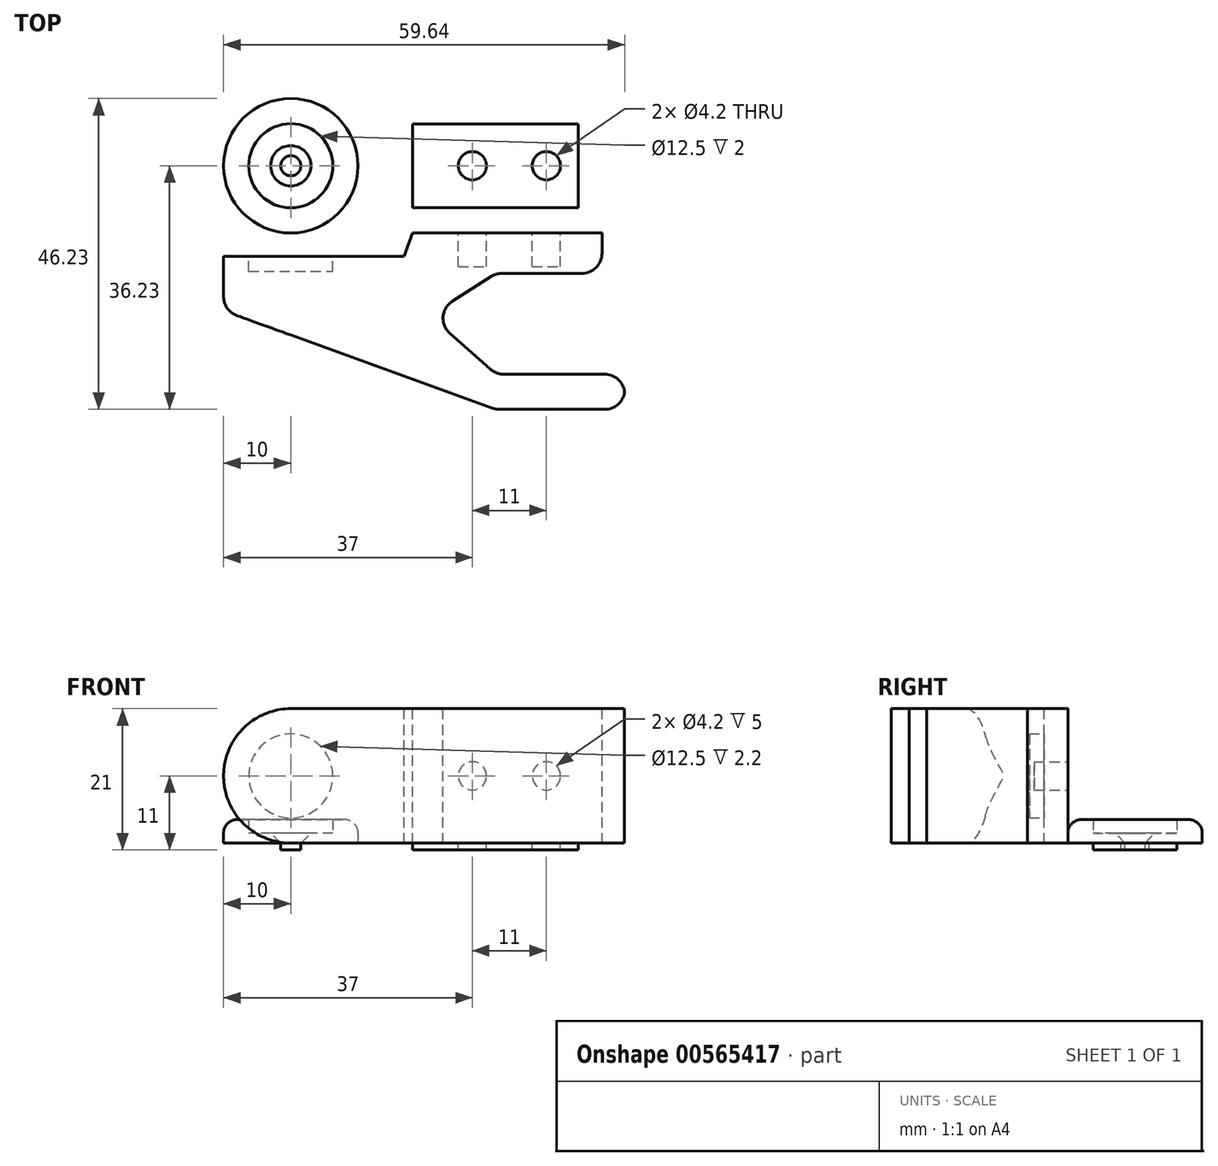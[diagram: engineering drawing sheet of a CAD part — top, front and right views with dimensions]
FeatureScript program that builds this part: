
annotation { "Feature Type Name" : "Feature", "Feature Type Description" : "" }
export const myFeature = defineFeature(function(context is Context, id is Id, definition is map)
    precondition{}
    {
        {
            var Q0;
            Q0=qCreatedBy(makeId("Top.planeOp"),FACE);
            var sketch = newSketch(context, id + "F0", { "sketchPlane" : qUnion([Q0])});
            skPoint(sketch, "E0", {"position": v(-15, 0) * mm});
            skPoint(sketch, "E1", {"position": v(15, 0) * mm});
            skCircle(sketch, "E2", {"center": v(-15, 0) * mm, "radius": 1.5 * mm});
            skCircle(sketch, "E3", {"center": v(-15, 0) * mm, "radius": 10 * mm});
            skCircle(sketch, "E4", {"center": v(-15, 0) * mm, "radius": 6.25 * mm});
            skSolve(sketch);
        }
        {
            var Q0;
            Q0=makeQuery(id+"F0.imprint","IMPRINT",FACE,{"disambiguationData":[TD([[makeQuery(id+"F0.imprint","IMPRINT",EDGE,{"derivedFrom":sQuery(id+"F0.wireOp",EDGE,"E3")}),1.0]])]});
            var Q1;
            Q1=makeQuery(id+"F0.imprint","IMPRINT",FACE,{"disambiguationData":[TD([[makeQuery(id+"F0.imprint","IMPRINT",EDGE,{"derivedFrom":sQuery(id+"F0.wireOp",EDGE,"E2")}),-1.0]])]});
            extrude(context, id + "F1", {"entities" : qUnion([Q0, Q1]), "depth" : 1.5 * mm, "offsetDistance" : 25 * mm});
        }
        {
            var Q0;
            Q0=makeQuery(id+"F1.opExtrude","CAP_EDGE",EDGE,{"disambiguationData":[OSD([sQuery(id+"F0.wireOp",EDGE,"E2")])],"isStart":false});
            chamfer(context, id + "F2", {"entities" : qUnion([Q0]), "width" : 1.5 * mm, "tangentPropagation" : true});
        }
        {
            var Q0;
            Q0=makeQuery(id+"F1.opExtrude","CAP_FACE",FACE,{"disambiguationData":[OSD([sQuery(id+"F0.wireOp",EDGE,"E2"),sQuery(id+"F0.wireOp",EDGE,"E3")])],"isStart":false});
            var sketch = newSketch(context, id + "F3", { "sketchPlane" : qUnion([Q0])});
            skCircle(sketch, "E5.0", {"center": v(-15, 0) * mm, "radius": 6.25 * mm});
            skCircle(sketch, "E6.0", {"center": v(-15, 0) * mm, "radius": 10 * mm});
            skSolve(sketch);
        }
        {
            var Q0;
            Q0=makeQuery(id+"F3.imprint","IMPRINT",FACE,{"disambiguationData":[TD([[makeQuery(id+"F3.imprint","IMPRINT",EDGE,{"derivedFrom":sQuery(id+"F3.wireOp",EDGE,"E5.0")}),-1.0]])]});
            extrude(context, id + "F4", {"entities" : qUnion([Q0]), "operationType" : NewBodyOperationType.ADD, "depth" : 2 * mm, "offsetDistance" : 25 * mm});
        }
        {
            var Q0;
            Q0=makeQuery(id+"F4.opExtrude","CAP_EDGE",EDGE,{"disambiguationData":[OSD([sQuery(id+"F3.wireOp",EDGE,"E6.0")])],"isStart":false});
            fillet(context, id + "F5", {"entities" : qUnion([Q0]), "radius" : 2 * mm, "tangentPropagation" : true, "allowEdgeOverflow" : false});
        }
        {
            var Q0;
            Q0=qCreatedBy(makeId("Front.planeOp"),FACE);
            var sketch = newSketch(context, id + "F6", { "sketchPlane" : qUnion([Q0])});
            skLineSegment(sketch, "E7.0", {"start": v(-23, 3.5) * mm, "end": v(-21.25, 3.5) * mm});
            skLineSegment(sketch, "E8", {"start": v(-23.02, 12.27) * mm, "end": v(15.04, 26.06) * mm});
            skLineSegment(sketch, "E9", {"start": v(16.06, 26.23) * mm, "end": v(31.66, 26.23) * mm});
            skLineSegment(sketch, "E10", {"start": v(34.66, 24) * mm, "end": v(34.66, 23.23) * mm});
            skLineSegment(sketch, "E11", {"start": v(31.66, 21) * mm, "end": v(16.67, 21) * mm});
            skLineSegment(sketch, "E12", {"start": v(14.68, 20.25) * mm, "end": v(8.65, 14.92) * mm});
            skLineSegment(sketch, "E13", {"start": v(9.03, 10.14) * mm, "end": v(14.8, 6.47) * mm});
            skLineSegment(sketch, "E14", {"start": v(16.4, 6) * mm, "end": v(28.27, 6) * mm});
            skLineSegment(sketch, "E15", {"start": v(31.27, 3) * mm, "end": v(31.27, 0) * mm});
            skLineSegment(sketch, "E16", {"start": v(31.27, 0) * mm, "end": v(3.08, 0) * mm});
            skLineSegment(sketch, "E17", {"start": v(3.08, 0) * mm, "end": v(1.81, 3.5) * mm});
            skLineSegment(sketch, "E18", {"start": v(1.81, 3.5) * mm, "end": v(-7, 3.5) * mm});
            skPoint(sketch, "E19.visualSharp", {"position": v(15.54, 21) * mm});
            skArc(sketch, "E19.filletArc", {"start": v(16.67, 21) * mm, "mid": v(15.6, 20.8) * mm, "end": v(14.68, 20.25) * mm});
            skPoint(sketch, "E20.visualSharp", {"position": v(5.66, 12.28) * mm});
            skArc(sketch, "E20.filletArc", {"start": v(8.65, 14.92) * mm, "mid": v(7.65, 12.43) * mm, "end": v(9.03, 10.14) * mm});
            skPoint(sketch, "E21.visualSharp", {"position": v(15.54, 6) * mm});
            skArc(sketch, "E21.filletArc", {"start": v(14.8, 6.47) * mm, "mid": v(15.57, 6.12) * mm, "end": v(16.4, 6) * mm});
            skPoint(sketch, "E22.visualSharp", {"position": v(31.27, 6) * mm});
            skArc(sketch, "E22.filletArc", {"start": v(31.27, 3) * mm, "mid": v(30.4, 5.12) * mm, "end": v(28.27, 6) * mm});
            skPoint(sketch, "E23.visualSharp", {"position": v(15.54, 26.23) * mm});
            skArc(sketch, "E23.filletArc", {"start": v(16.06, 26.23) * mm, "mid": v(15.54, 26.19) * mm, "end": v(15.04, 26.06) * mm});
            skPoint(sketch, "E24.visualSharp", {"position": v(-23, 12.28) * mm});
            skArc(sketch, "E24.filletArc", {"start": v(-23.02, 12.27) * mm, "mid": v(-24.46, 11.17) * mm, "end": v(-25, 9.45) * mm});
            skPoint(sketch, "E25.visualSharp", {"position": v(34.66, 26.23) * mm});
            skArc(sketch, "E25.filletArc", {"start": v(34.66, 23.23) * mm, "mid": v(33.78, 25.36) * mm, "end": v(31.66, 26.23) * mm});
            skPoint(sketch, "E26.visualSharp", {"position": v(34.66, 21) * mm});
            skArc(sketch, "E26.filletArc", {"start": v(31.66, 21) * mm, "mid": v(33.78, 21.88) * mm, "end": v(34.66, 24) * mm});
            skLineSegment(sketch, "E27", {"start": v(-8.75, 3.5) * mm, "end": v(-7, 3.5) * mm});
            skLineSegment(sketch, "E28", {"start": v(-21.25, 3.5) * mm, "end": v(-21.25, 5.7) * mm});
            skLineSegment(sketch, "E29", {"start": v(-21.25, 5.7) * mm, "end": v(-8.75, 5.7) * mm});
            skLineSegment(sketch, "E30", {"start": v(-8.75, 5.7) * mm, "end": v(-8.75, 3.5) * mm});
            skLineSegment(sketch, "E31", {"start": v(-21.25, 3.5) * mm, "end": v(-8.75, 3.5) * mm});
            skLineSegment(sketch, "E32", {"start": v(-25, 9.45) * mm, "end": v(-25, 3.5) * mm});
            skLineSegment(sketch, "E33.0", {"start": v(-25, 0) * mm, "end": v(-5, 0) * mm, "construction": true});
            skLineSegment(sketch, "E34", {"start": v(-25, 3.5) * mm, "end": v(-23, 3.5) * mm});
            skSolve(sketch);
        }
        {
            var Q0;
            Q0=makeQuery(id+"F6.imprint","IMPRINT",FACE,{"disambiguationData":[TD([[makeQuery(id+"F6.imprint","IMPRINT",EDGE,{"derivedFrom":sQuery(id+"F6.wireOp",EDGE,"E7.0")}),1.0]])]});
            var Q1;
            Q1=makeQuery(id+"F6.imprint","IMPRINT",FACE,{"disambiguationData":[TD([[makeQuery(id+"F6.imprint","IMPRINT",EDGE,{"derivedFrom":sQuery(id+"F6.wireOp",EDGE,"E28")}),-1.0]])]});
            extrude(context, id + "F7", {"entities" : qUnion([Q0, Q1]), "endBound" : BoundingType.SYMMETRIC, "depth" : 20 * mm, "offsetDistance" : 25 * mm});
        }
        {
            var Q0;
            Q0=makeQuery(id+"F7.opExtrude","SWEPT_FACE",FACE,{"disambiguationData":[OSD([sQuery(id+"F6.wireOp",EDGE,"E16")])]});
            var sketch = newSketch(context, id + "F8", { "sketchPlane" : qUnion([Q0])});
            skCircle(sketch, "E35", {"center": v(12, 0) * mm, "radius": 2.1 * mm});
            skPoint(sketch, "E35.centerSnap0", {"position": v(3.08, 0) * mm});
            skCircle(sketch, "E36", {"center": v(23, 0) * mm, "radius": 2.1 * mm});
            skSolve(sketch);
        }
        {
            var Q0;
            Q0=makeQuery(id+"F8.imprint","IMPRINT",FACE,{"disambiguationData":[TD([[makeQuery(id+"F8.imprint","IMPRINT",EDGE,{"derivedFrom":sQuery(id+"F8.wireOp",EDGE,"E35")}),1.0]])]});
            var Q1;
            Q1=makeQuery(id+"F8.imprint","IMPRINT",FACE,{"disambiguationData":[TD([[makeQuery(id+"F8.imprint","IMPRINT",EDGE,{"derivedFrom":sQuery(id+"F8.wireOp",EDGE,"E36")}),1.0]])]});
            extrude(context, id + "F9", {"entities" : qUnion([Q0, Q1]), "operationType" : NewBodyOperationType.REMOVE, "oppositeDirection" : true, "depth" : 5 * mm, "offsetDistance" : 25 * mm});
        }
        {
            var Q0;
            Q0=makeQuery(id+"F7.opExtrude","SWEPT_FACE",FACE,{"disambiguationData":[OSD([sQuery(id+"F6.wireOp",EDGE,"E7.0"),sQuery(id+"F6.wireOp",EDGE,"E18"),sQuery(id+"F6.wireOp",EDGE,"E27"),sQuery(id+"F6.wireOp",EDGE,"E31"),sQuery(id+"F6.wireOp",EDGE,"E34")])]});
            var sketch = newSketch(context, id + "F10", { "sketchPlane" : qUnion([Q0])});
            skCircle(sketch, "E37.0", {"center": v(-15, 0) * mm, "radius": 10 * mm});
            skCircle(sketch, "E38.0", {"center": v(-15, 0) * mm, "radius": 6.25 * mm});
            skSolve(sketch);
        }
        {
            var Q0;
            {var subQ0=sQuery(id+"F10.wireOp",EDGE,"E37.0");var subQ1=sQuery(id+"F6.wireOp",EDGE,"E34");var subQ2=makeQuery(id+"F7.opExtrude","SWEPT_EDGE",EDGE,{"disambiguationData":[OSD([sQuery(id+"F6.wireOp",EDGE,"E32"),subQ1])]});var subQ3=makeQuery(id+"F10.imprint","INTERSECT",VERTEX,{"derivedFrom":[subQ2,subQ0]});Q0=makeQuery(id+"F10.imprint","IMPRINT",FACE,{"disambiguationData":[TD([[makeQuery(id+"F10.imprint","IMPRINT",EDGE,{"disambiguationData":[TD([[subQ3,1.0]])],"derivedFrom":subQ0}),-1.0]])]});}
            var Q1;
            {var subQ0=sQuery(id+"F10.wireOp",EDGE,"E37.0");var subQ1=sQuery(id+"F6.wireOp",EDGE,"E34");var subQ2=makeQuery(id+"F7.opExtrude","SWEPT_EDGE",EDGE,{"disambiguationData":[OSD([sQuery(id+"F6.wireOp",EDGE,"E32"),subQ1])]});var subQ3=makeQuery(id+"F10.imprint","INTERSECT",VERTEX,{"derivedFrom":[subQ2,subQ0]});Q1=makeQuery(id+"F10.imprint","IMPRINT",FACE,{"disambiguationData":[TD([[makeQuery(id+"F10.imprint","IMPRINT",EDGE,{"disambiguationData":[TD([[subQ3,-1.0]])],"derivedFrom":subQ0}),-1.0]])]});}
            extrude(context, id + "F11", {"entities" : qUnion([Q0, Q1]), "operationType" : NewBodyOperationType.REMOVE, "endBound" : BoundingType.THROUGH_ALL, "oppositeDirection" : true, "depth" : 25 * mm, "offsetDistance" : 25 * mm});
        }
        {
            var Q0;
            Q0=makeQuery(id+"F10.imprint","IMPRINT",FACE,{"disambiguationData":[TD([[makeQuery(id+"F10.imprint","IMPRINT",EDGE,{"derivedFrom":sQuery(id+"F10.wireOp",EDGE,"E38.0")}),1.0]])]});
            extrude(context, id + "F12", {"entities" : qUnion([Q0]), "operationType" : NewBodyOperationType.REMOVE, "oppositeDirection" : true, "depth" : 2.2 * mm, "offsetDistance" : 25 * mm});
        }
        {
            var Q0;
            Q0=makeQuery(id+"F7.opExtrude","SWEPT_FACE",FACE,{"disambiguationData":[OSD([sQuery(id+"F6.wireOp",EDGE,"E16")])]});
            var sketch = newSketch(context, id + "F13", { "sketchPlane" : qUnion([Q0])});
            skCircle(sketch, "E39.0", {"center": v(-15, 0) * mm, "radius": 1.5 * mm});
            skCircle(sketch, "E40.0", {"center": v(12, 0) * mm, "radius": 2.1 * mm, "construction": true});
            skCircle(sketch, "E41.0", {"center": v(23, 0) * mm, "radius": 2.1 * mm, "construction": true});
            skLineSegment(sketch, "E42", {"start": v(0, 6.2) * mm, "end": v(27.78, 6.2) * mm});
            skLineSegment(sketch, "E43", {"start": v(27.78, 6.2) * mm, "end": v(27.78, -6.2) * mm});
            skLineSegment(sketch, "E44", {"start": v(27.78, -6.2) * mm, "end": v(0, -6.2) * mm});
            skLineSegment(sketch, "E45", {"start": v(0, -6.2) * mm, "end": v(0, -3.36) * mm});
            skLineSegment(sketch, "E46", {"start": v(0, -3.36) * mm, "end": v(-19.29, -3.36) * mm});
            skLineSegment(sketch, "E47", {"start": v(-19.29, -3.36) * mm, "end": v(-19.29, 3.36) * mm});
            skLineSegment(sketch, "E48", {"start": v(-19.29, 3.36) * mm, "end": v(0, 3.36) * mm});
            skLineSegment(sketch, "E49", {"start": v(0, 3.36) * mm, "end": v(0, 6.2) * mm});
            skPoint(sketch, "E50", {"position": v(-19.29, 0) * mm});
            skCircle(sketch, "E51", {"center": v(12, 0) * mm, "radius": 1.5 * mm});
            skCircle(sketch, "E52", {"center": v(23, 0) * mm, "radius": 1.5 * mm});
            skSolve(sketch);
        }
        {
            var Q0;
            Q0=makeQuery(id+"F13.imprint","IMPRINT",FACE,{"disambiguationData":[TD([[makeQuery(id+"F13.imprint","IMPRINT",EDGE,{"derivedFrom":sQuery(id+"F13.wireOp",EDGE,"E39.0")}),1.0]])]});
            var Q1;
            {var subQ1=sQuery(id+"F13.wireOp",EDGE,"E43");Q1=makeQuery(id+"F13.imprint","IMPRINT",FACE,{"disambiguationData":[TD([[makeQuery(id+"F13.imprint","IMPRINT",EDGE,{"derivedFrom":subQ1}),-1.0]])]});}
            extrude(context, id + "F14", {"entities" : qUnion([Q0, Q1]), "depth" : 1 * mm, "offsetDistance" : 25 * mm});
        }
        {
            var Q0;
            Q0=makeQuery(id+"F7.opExtrude","SWEPT_BODY",BODY,{"disambiguationData":[OSD([sQuery(id+"F6.wireOp",EDGE,"E7.0"),sQuery(id+"F6.wireOp",EDGE,"E8"),sQuery(id+"F6.wireOp",EDGE,"E9"),sQuery(id+"F6.wireOp",EDGE,"E11"),sQuery(id+"F6.wireOp",EDGE,"E12"),sQuery(id+"F6.wireOp",EDGE,"E13"),sQuery(id+"F6.wireOp",EDGE,"E14"),sQuery(id+"F6.wireOp",EDGE,"E15"),sQuery(id+"F6.wireOp",EDGE,"E16"),sQuery(id+"F6.wireOp",EDGE,"E17"),sQuery(id+"F6.wireOp",EDGE,"E18"),sQuery(id+"F6.wireOp",EDGE,"E19.filletArc"),sQuery(id+"F6.wireOp",EDGE,"E20.filletArc"),sQuery(id+"F6.wireOp",EDGE,"E21.filletArc"),sQuery(id+"F6.wireOp",EDGE,"E22.filletArc"),sQuery(id+"F6.wireOp",EDGE,"E23.filletArc"),sQuery(id+"F6.wireOp",EDGE,"E24.filletArc"),sQuery(id+"F6.wireOp",EDGE,"E25.filletArc"),sQuery(id+"F6.wireOp",EDGE,"E26.filletArc"),sQuery(id+"F6.wireOp",EDGE,"E27"),sQuery(id+"F6.wireOp",EDGE,"E31"),sQuery(id+"F6.wireOp",EDGE,"E32"),sQuery(id+"F6.wireOp",EDGE,"E34")])]});
            var Q1;
            Q1=makeQuery(id+"F7.opExtrude","CAP_EDGE",EDGE,{"disambiguationData":[OSD([sQuery(id+"F6.wireOp",EDGE,"E16")])],"isStart":false});
            transform(context, id + "F15", {"entities" : qUnion([Q0]), "transformType" : TransformType.ROTATION, "transformAxis" : qUnion([Q1]), "angle" : 90 * degree, "oppositeDirection" : true, "makeCopy" : false});
        }
    });
